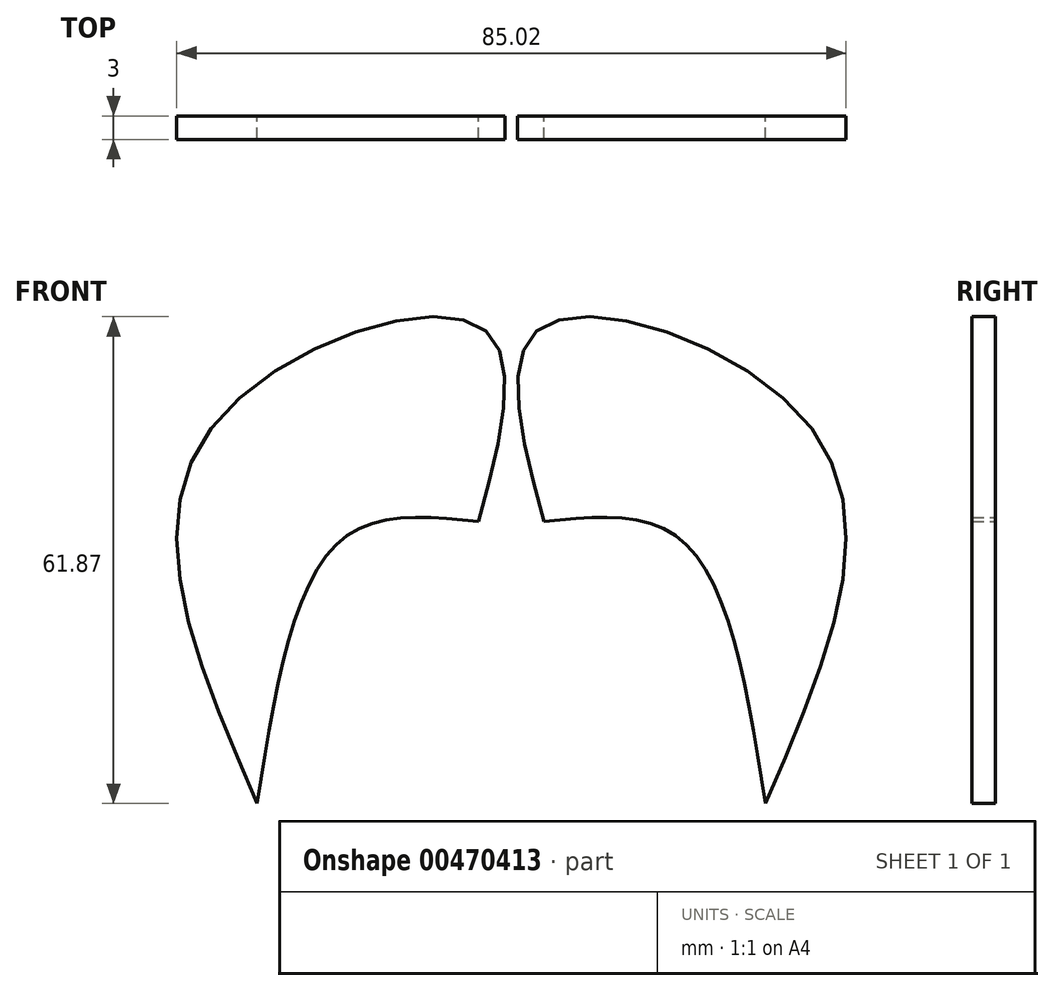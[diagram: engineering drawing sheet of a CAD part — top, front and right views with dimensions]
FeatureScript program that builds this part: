
annotation { "Feature Type Name" : "Feature", "Feature Type Description" : "" }
export const myFeature = defineFeature(function(context is Context, id is Id, definition is map)
    precondition{}
    {
        {
            var Q0;
            Q0=qCreatedBy(makeId("Front.planeOp"),FACE);
            var sketch = newSketch(context, id + "F0", { "sketchPlane" : qUnion([Q0])});
            skFitSpline(sketch, "E0", {"points": [v(-4.14, 16.88) * mm, v(-4.14, 41.74) * mm, v(-38.78, 27.83) * mm, v(-32.27, -18.95) * mm], "startDerivative": vector(31.2, 116.37) * mm, "endDerivative": vector(58.62, -135.17) * mm});
            skFitSpline(sketch, "E1", {"points": [v(-32.27, -18.95) * mm, v(-21.61, 14.5) * mm, v(-4.14, 16.88) * mm], "startDerivative": vector(11.21, 72.21) * mm, "endDerivative": vector(47.08, -4.96) * mm});
            skFitSpline(sketch, "E2.MirrorCS", {"points": [v(4.14, 16.88) * mm, v(4.14, 41.74) * mm, v(38.78, 27.83) * mm, v(32.27, -18.95) * mm], "startDerivative": vector(-31.2, 116.37) * mm, "endDerivative": vector(-58.62, -135.17) * mm});
            skFitSpline(sketch, "E3.MirrorCS", {"points": [v(32.27, -18.95) * mm, v(21.61, 14.5) * mm, v(4.14, 16.88) * mm], "startDerivative": vector(-11.21, 72.21) * mm, "endDerivative": vector(-47.08, -4.96) * mm});
            skSolve(sketch);
        }
        {
            var Q0;
            Q0=makeQuery(id+"F0.imprint","IMPRINT",FACE,{"disambiguationData":[TD([[makeQuery(id+"F0.imprint","IMPRINT",EDGE,{"derivedFrom":sQuery(id+"F0.wireOp",EDGE,"E2.MirrorCS")}),-1.0]])]});
            var Q1;
            Q1=makeQuery(id+"F0.imprint","IMPRINT",FACE,{"disambiguationData":[TD([[makeQuery(id+"F0.imprint","IMPRINT",EDGE,{"derivedFrom":sQuery(id+"F0.wireOp",EDGE,"E0")}),1.0]])]});
            extrude(context, id + "F1", {"entities" : qUnion([Q0, Q1]), "depth" : 3 * mm});
        }
    });
